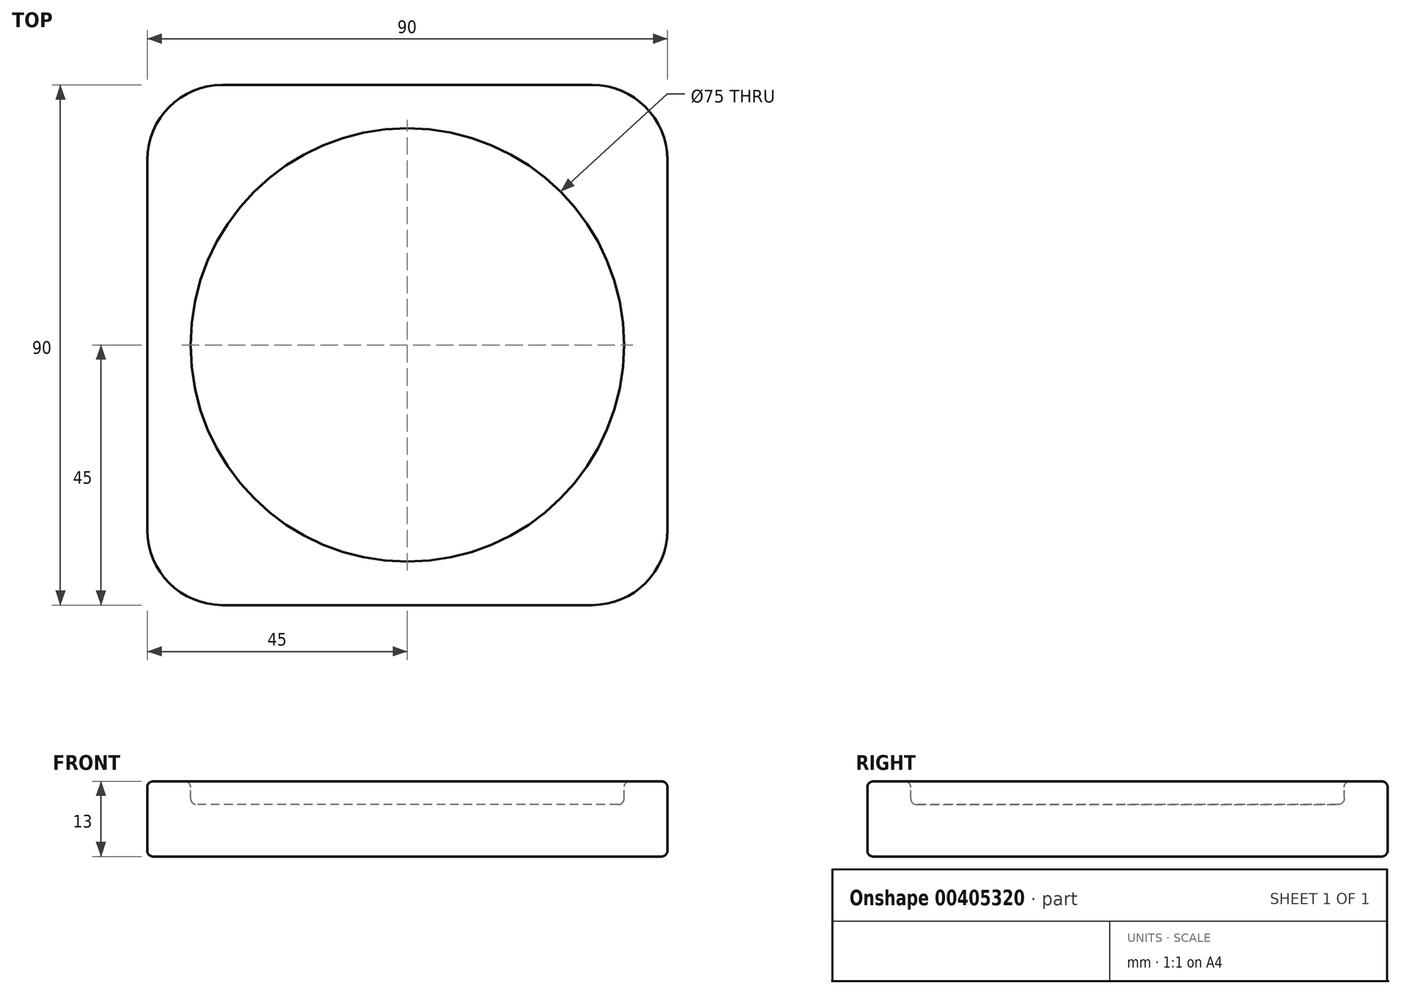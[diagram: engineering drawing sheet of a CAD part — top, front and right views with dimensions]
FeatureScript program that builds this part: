
annotation { "Feature Type Name" : "Feature", "Feature Type Description" : "" }
export const myFeature = defineFeature(function(context is Context, id is Id, definition is map)
    precondition{}
    {
        {
            var Q0;
            Q0=qCreatedBy(makeId("Top.planeOp"),FACE);
            var sketch = newSketch(context, id + "F0", { "sketchPlane" : qUnion([Q0])});
            skLineSegment(sketch, "E0.bottom", {"start": v(45, 45) * mm, "end": v(-45, 45) * mm});
            skLineSegment(sketch, "E0.top", {"start": v(45, -45) * mm, "end": v(-45, -45) * mm});
            skLineSegment(sketch, "E0.left", {"start": v(45, 45) * mm, "end": v(45, -45) * mm});
            skLineSegment(sketch, "E0.right", {"start": v(-45, 45) * mm, "end": v(-45, -45) * mm});
            skPoint(sketch, "E0.middle", {"position": v(0, 0) * mm});
            skSolve(sketch);
        }
        {
            var Q0;
            Q0=makeQuery(id+"F0.imprint","IMPRINT",FACE,{"disambiguationData":[TD([[makeQuery(id+"F0.imprint","IMPRINT",EDGE,{"derivedFrom":sQuery(id+"F0.wireOp",EDGE,"E0.bottom")}),1.0]])]});
            extrude(context, id + "F1", {"entities" : qUnion([Q0]), "depth" : 13 * mm});
        }
        {
            var Q0;
            Q0=makeQuery(id+"F1.opExtrude","CAP_FACE",FACE,{"disambiguationData":[OSD([sQuery(id+"F0.wireOp",EDGE,"E0.bottom"),sQuery(id+"F0.wireOp",EDGE,"E0.top"),sQuery(id+"F0.wireOp",EDGE,"E0.left"),sQuery(id+"F0.wireOp",EDGE,"E0.right")])],"isStart":false});
            var sketch = newSketch(context, id + "F2", { "sketchPlane" : qUnion([Q0])});
            skCircle(sketch, "E1", {"center": v(0, 0) * mm, "radius": 37.5 * mm});
            skSolve(sketch);
        }
        {
            var Q0;
            Q0=makeQuery(id+"F2.imprint","IMPRINT",FACE,{"disambiguationData":[TD([[makeQuery(id+"F2.imprint","IMPRINT",EDGE,{"derivedFrom":sQuery(id+"F2.wireOp",EDGE,"E1")}),1.0]])]});
            extrude(context, id + "F3", {"entities" : qUnion([Q0]), "operationType" : NewBodyOperationType.REMOVE, "oppositeDirection" : true, "depth" : 4 * mm});
        }
        {
            var Q0;
            Q0=makeQuery(id+"F1.opExtrude","SWEPT_EDGE",EDGE,{"disambiguationData":[OSD([sQuery(id+"F0.wireOp",EDGE,"E0.bottom"),sQuery(id+"F0.wireOp",EDGE,"E0.left")])]});
            var Q1;
            Q1=makeQuery(id+"F1.opExtrude","SWEPT_EDGE",EDGE,{"disambiguationData":[OSD([sQuery(id+"F0.wireOp",EDGE,"E0.bottom"),sQuery(id+"F0.wireOp",EDGE,"E0.right")])]});
            var Q2;
            Q2=makeQuery(id+"F1.opExtrude","SWEPT_EDGE",EDGE,{"disambiguationData":[OSD([sQuery(id+"F0.wireOp",EDGE,"E0.top"),sQuery(id+"F0.wireOp",EDGE,"E0.right")])]});
            var Q3;
            Q3=makeQuery(id+"F1.opExtrude","SWEPT_EDGE",EDGE,{"disambiguationData":[OSD([sQuery(id+"F0.wireOp",EDGE,"E0.top"),sQuery(id+"F0.wireOp",EDGE,"E0.left")])]});
            fillet(context, id + "F4", {"entities" : qUnion([Q0, Q1, Q2, Q3]), "radius" : 13 * mm, "tangentPropagation" : true, "allowEdgeOverflow" : false});
        }
        {
            var Q0;
            Q0=makeQuery(id+"F1.opExtrude","CAP_EDGE",EDGE,{"disambiguationData":[OSD([sQuery(id+"F0.wireOp",EDGE,"E0.left")])],"isStart":false});
            var Q1;
            Q1=makeQuery(id+"F1.opExtrude","CAP_EDGE",EDGE,{"disambiguationData":[OSD([sQuery(id+"F0.wireOp",EDGE,"E0.bottom")])],"isStart":true});
            var Q2;
            Q2=makeQuery(id+"F3.boolean.opBoolean","COPY",FACE,{"derivedFrom":makeQuery(id+"F3.opExtrude","SWEPT_FACE",FACE,{"disambiguationData":[OSD([sQuery(id+"F2.wireOp",EDGE,"E1")])]})});
            fillet(context, id + "F5", {"entities" : qUnion([Q0, Q1, Q2]), "radius" : 1 * mm, "tangentPropagation" : true, "allowEdgeOverflow" : false});
        }
    });
